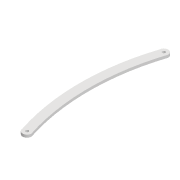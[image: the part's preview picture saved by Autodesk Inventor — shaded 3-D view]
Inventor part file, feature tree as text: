
AUTODESK INVENTOR PART (.ipt)
format: ipt  version: 2022 (Build 260153000, 153)  size: 94,208 bytes
history: native  units: mm
features: extrude x1, sketch x1
ambient origin geometry x8: Origin, YZ Plane, XZ Plane, XY Plane, X Axis, Y Axis, Z Axis, Center Point
bodies: Solid1 (feature_tree)
feature tree (2):
  extrude  "Extrusion1"  Depth=250.0mm
  sketch  "Sketch1"  dims[d0=3.3mm d1=3.3mm d2=10.0mm d3=153.584mm d6=3.0mm d7=0.0mm d12=250.0mm d13=250.0mm]
